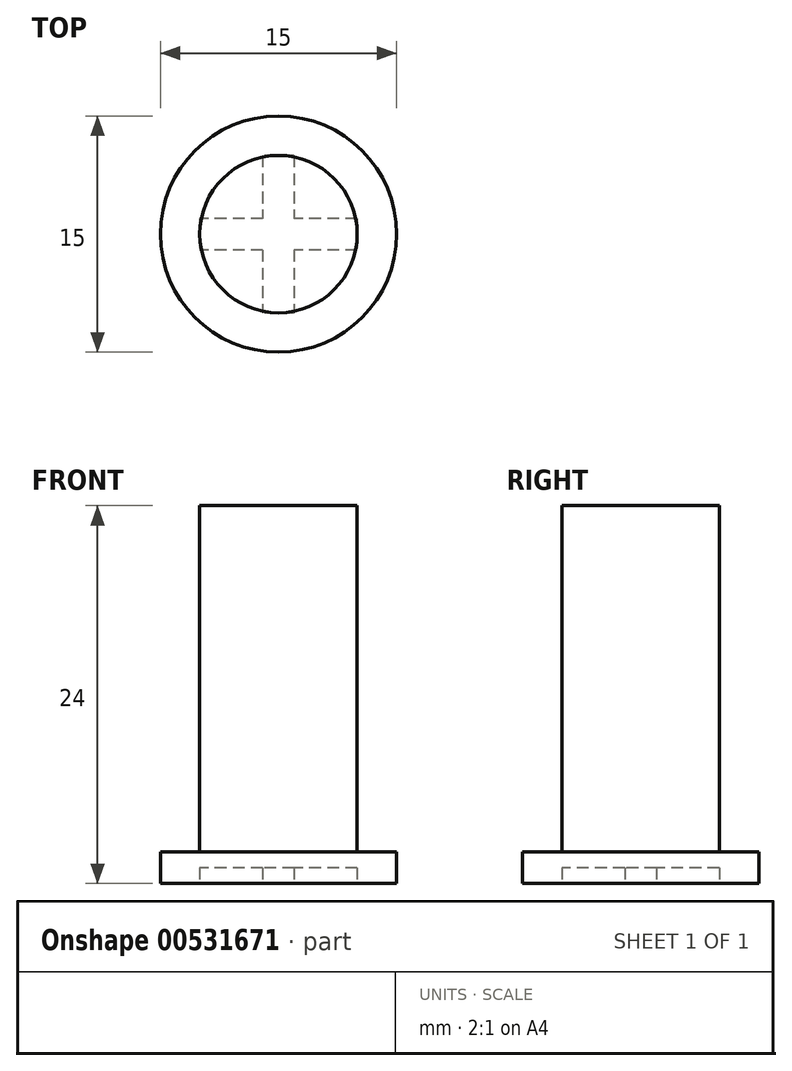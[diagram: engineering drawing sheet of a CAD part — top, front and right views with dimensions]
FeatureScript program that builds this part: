
annotation { "Feature Type Name" : "Feature", "Feature Type Description" : "" }
export const myFeature = defineFeature(function(context is Context, id is Id, definition is map)
    precondition{}
    {
        {
            var Q0;
            Q0=qCreatedBy(makeId("Top.planeOp"),FACE);
            var sketch = newSketch(context, id + "F0", { "sketchPlane" : qUnion([Q0])});
            skCircle(sketch, "E0", {"center": v(0, 0) * mm, "radius": 7.5 * mm});
            skSolve(sketch);
        }
        {
            var Q0;
            Q0=makeQuery(id+"F0.imprint","IMPRINT",FACE,{"disambiguationData":[TD([[makeQuery(id+"F0.imprint","IMPRINT",EDGE,{"derivedFrom":sQuery(id+"F0.wireOp",EDGE,"E0")}),1.0]])]});
            extrude(context, id + "F1", {"entities" : qUnion([Q0]), "depth" : 2 * mm, "offsetDistance" : 25 * mm});
        }
        {
            var Q0;
            Q0=makeQuery(id+"F1.opExtrude","CAP_FACE",FACE,{"disambiguationData":[OSD([sQuery(id+"F0.wireOp",EDGE,"E0")])],"isStart":false});
            var sketch = newSketch(context, id + "F2", { "sketchPlane" : qUnion([Q0])});
            skCircle(sketch, "E1", {"center": v(0, 0) * mm, "radius": 5 * mm});
            skSolve(sketch);
        }
        {
            var Q0;
            Q0=qSketchRegion(id+"F2",true);
            extrude(context, id + "F3", {"entities" : qUnion([Q0]), "operationType" : NewBodyOperationType.ADD, "flatOperationType" : FlatOperationType.REMOVE, "depth" : 22 * mm, "offsetDistance" : 25 * mm, "domain" : OperationDomain.MODEL});
        }
        {
            var Q0;
            Q0=makeQuery(id+"F1.opExtrude","CAP_FACE",FACE,{"disambiguationData":[OSD([sQuery(id+"F0.wireOp",EDGE,"E0")])],"isStart":true});
            var sketch = newSketch(context, id + "F4", { "sketchPlane" : qUnion([Q0])});
            skLineSegment(sketch, "E2.bottom", {"start": v(5, -1) * mm, "end": v(-5, -1) * mm});
            skLineSegment(sketch, "E2.top", {"start": v(5, 1) * mm, "end": v(-5, 1) * mm});
            skLineSegment(sketch, "E2.left", {"start": v(5, -1) * mm, "end": v(5, 1) * mm});
            skLineSegment(sketch, "E2.right", {"start": v(-5, -1) * mm, "end": v(-5, 1) * mm});
            skPoint(sketch, "E2.middle", {"position": v(0, 0) * mm});
            skLineSegment(sketch, "E3.bottom", {"start": v(1, -5) * mm, "end": v(-1, -5) * mm});
            skLineSegment(sketch, "E3.top", {"start": v(1, 5) * mm, "end": v(-1, 5) * mm});
            skLineSegment(sketch, "E3.left", {"start": v(1, -5) * mm, "end": v(1, 5) * mm});
            skLineSegment(sketch, "E3.right", {"start": v(-1, -5) * mm, "end": v(-1, 5) * mm});
            skSolve(sketch);
        }
        {
            var Q0;
            Q0=qSketchRegion(id+"F4",true);
            extrude(context, id + "F5", {"entities" : qUnion([Q0]), "operationType" : NewBodyOperationType.REMOVE, "oppositeDirection" : true, "depth" : 1 * mm});
        }
    });
